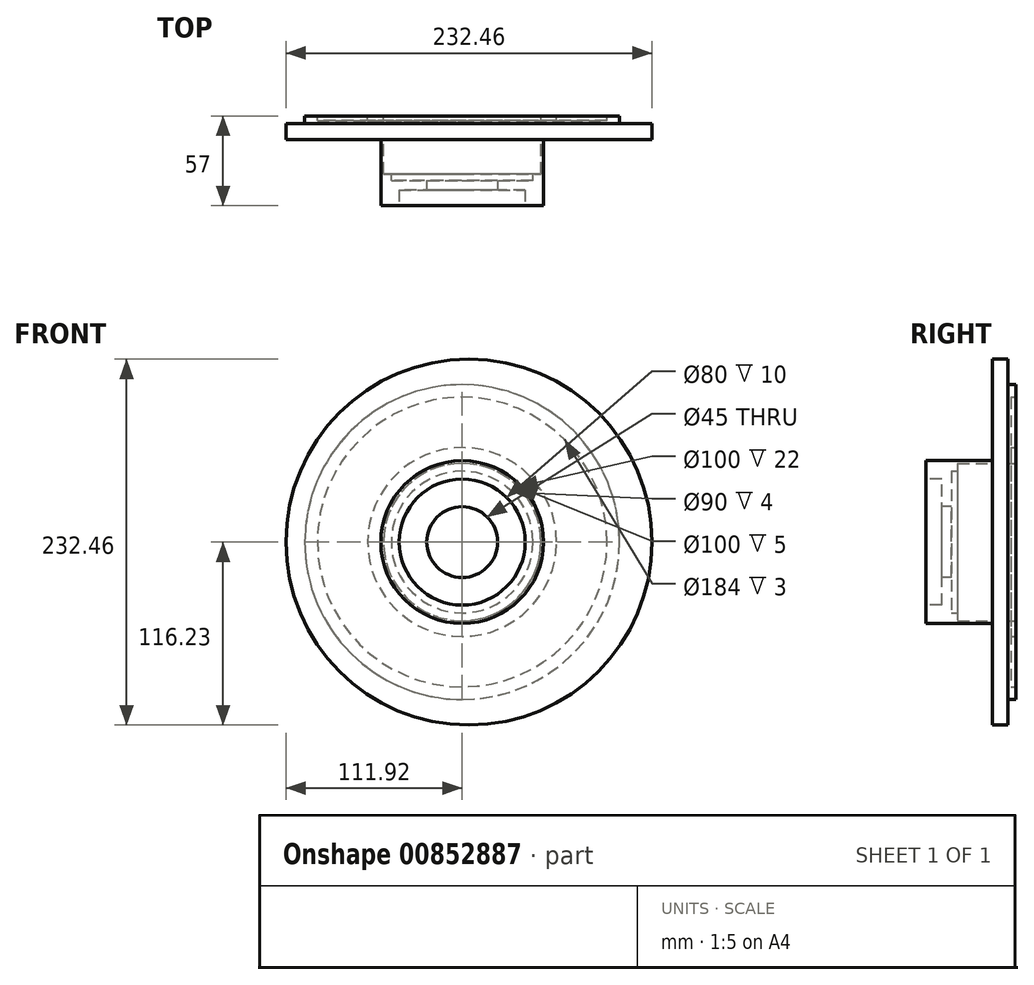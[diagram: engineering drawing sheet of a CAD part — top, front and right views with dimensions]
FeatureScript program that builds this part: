
annotation { "Feature Type Name" : "Feature", "Feature Type Description" : "" }
export const myFeature = defineFeature(function(context is Context, id is Id, definition is map)
    precondition{}
    {
        {
            var Q0;
            Q0=qCreatedBy(makeId("Front.planeOp"),FACE);
            var sketch = newSketch(context, id + "F0", { "sketchPlane" : qUnion([Q0])});
            skCircle(sketch, "E0", {"center": v(0, 0) * mm, "radius": 51.7 * mm});
            skCircle(sketch, "E1", {"center": v(0, 0) * mm, "radius": 22.5 * mm});
            skCircle(sketch, "E2", {"center": v(0, 0) * mm, "radius": 40 * mm});
            skSolve(sketch);
        }
        {
            var Q0;
            Q0=makeQuery(id+"F0.imprint","IMPRINT",FACE,{"disambiguationData":[TD([[makeQuery(id+"F0.imprint","IMPRINT",EDGE,{"derivedFrom":sQuery(id+"F0.wireOp",EDGE,"E0")}),1.0]])]});
            var Q1;
            Q1=makeQuery(id+"F0.imprint","IMPRINT",FACE,{"disambiguationData":[TD([[makeQuery(id+"F0.imprint","IMPRINT",EDGE,{"derivedFrom":sQuery(id+"F0.wireOp",EDGE,"RjNP8cjw-jCsV-HnkT-56pr-s8U0XfYvmQbq")}),1.0]])]});
            var Q2;
            Q2=makeQuery(id+"F0.imprint","IMPRINT",FACE,{"disambiguationData":[TD([[makeQuery(id+"F0.imprint","IMPRINT",EDGE,{"derivedFrom":sQuery(id+"F0.wireOp",EDGE,"0SzQyE8R-LriZ-WUbR-JEcH-lsWzORez8OF9")}),1.0]])]});
            var Q3;
            Q3=makeQuery(id+"F0.imprint","IMPRINT",FACE,{"disambiguationData":[TD([[makeQuery(id+"F0.imprint","IMPRINT",EDGE,{"derivedFrom":sQuery(id+"F0.wireOp",EDGE,"E1")}),-1.0]])]});
            var Q4;
            Q4=makeQuery(id+"F0.imprint","IMPRINT",FACE,{"disambiguationData":[TD([[makeQuery(id+"F0.imprint","IMPRINT",EDGE,{"derivedFrom":sQuery(id+"F0.wireOp",EDGE,"E1")}),1.0]])]});
            extrude(context, id + "F1", {"entities" : qUnion([Q0, Q1, Q2, Q3, Q4]), "oppositeDirection" : true, "depth" : 57 * mm, "offsetDistance" : 25 * mm});
        }
        {
            var Q0;
            Q0=makeQuery(id+"F0.imprint","IMPRINT",FACE,{"disambiguationData":[TD([[makeQuery(id+"F0.imprint","IMPRINT",EDGE,{"derivedFrom":sQuery(id+"F0.wireOp",EDGE,"E1")}),-1.0]])]});
            extrude(context, id + "F2", {"entities" : qUnion([Q0]), "operationType" : NewBodyOperationType.REMOVE, "oppositeDirection" : true, "depth" : 10 * mm, "offsetDistance" : 25 * mm});
        }
        {
            var Q0;
            Q0=makeQuery(id+"F0.imprint","IMPRINT",FACE,{"disambiguationData":[TD([[makeQuery(id+"F0.imprint","IMPRINT",EDGE,{"derivedFrom":sQuery(id+"F0.wireOp",EDGE,"E1")}),1.0]])]});
            extrude(context, id + "F3", {"entities" : qUnion([Q0]), "operationType" : NewBodyOperationType.REMOVE, "oppositeDirection" : true, "depth" : 16 * mm, "offsetDistance" : 25 * mm});
        }
        {
            var Q0;
            Q0=makeQuery(id+"F1.opExtrude","CAP_FACE",FACE,{"disambiguationData":[OSD([sQuery(id+"F0.wireOp",EDGE,"E0")])],"isStart":false});
            var sketch = newSketch(context, id + "F4", { "sketchPlane" : qUnion([Q0])});
            skCircle(sketch, "E3", {"center": v(0, 0) * mm, "radius": 45 * mm});
            skCircle(sketch, "E4", {"center": v(0, 0) * mm, "radius": 50 * mm});
            skCircle(sketch, "E5", {"center": v(0, 0) * mm, "radius": 92 * mm});
            skCircle(sketch, "E6", {"center": v(0, 0) * mm, "radius": 100 * mm});
            skCircle(sketch, "E7", {"center": v(0, 0) * mm, "radius": 60 * mm});
            skSolve(sketch);
        }
        {
            var Q0;
            Q0=makeQuery(id+"F4.imprint","IMPRINT",FACE,{"disambiguationData":[TD([[makeQuery(id+"F4.imprint","IMPRINT",EDGE,{"derivedFrom":sQuery(id+"F4.wireOp",EDGE,"E3")}),-1.0]])]});
            extrude(context, id + "F5", {"entities" : qUnion([Q0]), "operationType" : NewBodyOperationType.REMOVE, "oppositeDirection" : true, "depth" : 37 * mm, "offsetDistance" : 25 * mm});
        }
        {
            var Q0;
            Q0=makeQuery(id+"F4.imprint","IMPRINT",FACE,{"disambiguationData":[TD([[makeQuery(id+"F4.imprint","IMPRINT",EDGE,{"derivedFrom":sQuery(id+"F4.wireOp",EDGE,"E3")}),1.0]])]});
            extrude(context, id + "F6", {"entities" : qUnion([Q0]), "operationType" : NewBodyOperationType.REMOVE, "oppositeDirection" : true, "depth" : 41 * mm, "offsetDistance" : 25 * mm});
        }
        {
            var Q0;
            Q0=makeQuery(id+"F4.imprint","IMPRINT",FACE,{"disambiguationData":[TD([[makeQuery(id+"F4.imprint","IMPRINT",EDGE,{"derivedFrom":sQuery(id+"F4.wireOp",EDGE,"E5")}),-1.0]])]});
            var Q1;
            Q1=makeQuery(id+"F4.imprint","IMPRINT",FACE,{"disambiguationData":[TD([[makeQuery(id+"F4.imprint","IMPRINT",EDGE,{"derivedFrom":sQuery(id+"F4.wireOp",EDGE,"E5")}),1.0]])]});
            var Q2;
            Q2=makeQuery(id+"F4.imprint","IMPRINT",FACE,{"disambiguationData":[TD([[makeQuery(id+"F4.imprint","IMPRINT",EDGE,{"derivedFrom":sQuery(id+"F4.wireOp",EDGE,"E7")}),1.0]])]});
            extrude(context, id + "F7", {"entities" : qUnion([Q0, Q1, Q2]), "operationType" : NewBodyOperationType.ADD, "oppositeDirection" : true, "depth" : 5 * mm, "offsetDistance" : 25 * mm});
        }
        {
            var Q0;
            Q0=makeQuery(id+"F4.imprint","IMPRINT",FACE,{"disambiguationData":[TD([[makeQuery(id+"F4.imprint","IMPRINT",EDGE,{"derivedFrom":sQuery(id+"F4.wireOp",EDGE,"E5")}),1.0]])]});
            extrude(context, id + "F8", {"entities" : qUnion([Q0]), "operationType" : NewBodyOperationType.REMOVE, "oppositeDirection" : true, "depth" : 3 * mm, "offsetDistance" : 25 * mm});
        }
        {
            var Q0;
            Q0=makeQuery(id+"F7.opExtrude","CAP_FACE",FACE,{"disambiguationData":[OSD([sQuery(id+"F0.wireOp",EDGE,"E0"),sQuery(id+"F4.wireOp",EDGE,"E6")])],"isStart":false});
            var sketch = newSketch(context, id + "F9", { "sketchPlane" : qUnion([Q0])});
            skCircle(sketch, "E8", {"center": v(4.31, 0) * mm, "radius": 116.23 * mm});
            skSolve(sketch);
        }
        {
            var Q0;
            Q0 = qSketchRegion(id + "F9", true);
            extrude(context, id + "F10", {"entities" : qUnion([Q0]), "operationType" : NewBodyOperationType.ADD, "depth" : 10 * mm, "offsetDistance" : 25 * mm});
        }
    });
